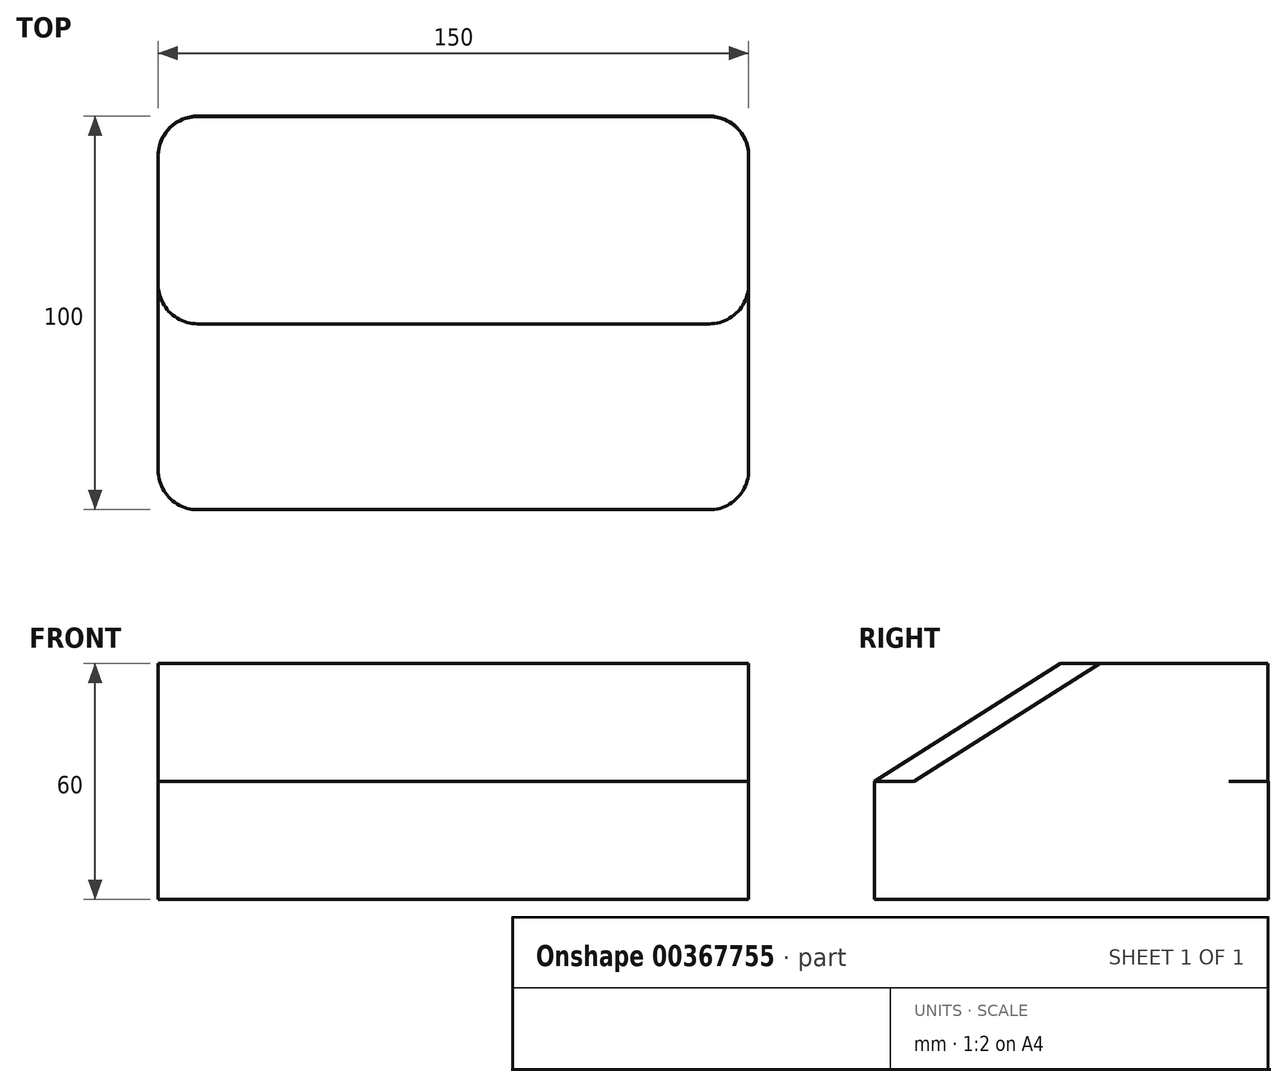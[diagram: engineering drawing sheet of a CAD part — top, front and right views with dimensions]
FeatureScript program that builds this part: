
annotation { "Feature Type Name" : "Feature", "Feature Type Description" : "" }
export const myFeature = defineFeature(function(context is Context, id is Id, definition is map)
    precondition{}
    {
        {
            var Q0;
            Q0=qCreatedBy(makeId("Top.planeOp"),FACE);
            var sketch = newSketch(context, id + "F0", { "sketchPlane" : qUnion([Q0])});
            skLineSegment(sketch, "E0.bottom", {"start": v(-67.57, 52.77) * mm, "end": v(62.43, 52.77) * mm});
            skLineSegment(sketch, "E0.top", {"start": v(-67.57, -47.23) * mm, "end": v(62.43, -47.23) * mm});
            skLineSegment(sketch, "E0.left", {"start": v(-77.57, 42.77) * mm, "end": v(-77.57, -37.23) * mm});
            skLineSegment(sketch, "E0.right", {"start": v(72.43, 42.77) * mm, "end": v(72.43, -37.23) * mm});
            skPoint(sketch, "E1.visualSharp", {"position": v(-77.57, 52.77) * mm});
            skArc(sketch, "E1.filletArc", {"start": v(-67.57, 52.77) * mm, "mid": v(-74.64, 49.85) * mm, "end": v(-77.57, 42.77) * mm});
            skPoint(sketch, "E2.visualSharp", {"position": v(72.43, 52.77) * mm});
            skArc(sketch, "E2.filletArc", {"start": v(72.43, 42.77) * mm, "mid": v(69.5, 49.85) * mm, "end": v(62.43, 52.77) * mm});
            skPoint(sketch, "E3.visualSharp", {"position": v(72.43, -47.23) * mm});
            skArc(sketch, "E3.filletArc", {"start": v(62.43, -47.23) * mm, "mid": v(69.5, -44.3) * mm, "end": v(72.43, -37.23) * mm});
            skPoint(sketch, "E4.visualSharp", {"position": v(-77.57, -47.23) * mm});
            skArc(sketch, "E4.filletArc", {"start": v(-77.57, -37.23) * mm, "mid": v(-74.64, -44.3) * mm, "end": v(-67.57, -47.23) * mm});
            skSolve(sketch);
        }
        {
            var Q0;
            Q0=makeQuery(id+"F0.imprint","IMPRINT",FACE,{"disambiguationData":[TD([[makeQuery(id+"F0.imprint","IMPRINT",EDGE,{"derivedFrom":sQuery(id+"F0.wireOp",EDGE,"E0.bottom")}),-1.0]])]});
            extrude(context, id + "F1", {"entities" : qUnion([Q0]), "depth" : 30 * mm});
        }
        {
            var Q0;
            Q0=makeQuery(id+"F1.opExtrude","CAP_FACE",FACE,{"disambiguationData":[OSD([sQuery(id+"F0.wireOp",EDGE,"E0.bottom"),sQuery(id+"F0.wireOp",EDGE,"E0.top"),sQuery(id+"F0.wireOp",EDGE,"E0.left"),sQuery(id+"F0.wireOp",EDGE,"E0.right"),sQuery(id+"F0.wireOp",EDGE,"E1.filletArc"),sQuery(id+"F0.wireOp",EDGE,"E2.filletArc"),sQuery(id+"F0.wireOp",EDGE,"E3.filletArc"),sQuery(id+"F0.wireOp",EDGE,"E4.filletArc")])],"isStart":false});
            var sketch = newSketch(context, id + "F2", { "sketchPlane" : qUnion([Q0])});
            skLineSegment(sketch, "E5.bottom", {"start": v(-67.57, 52.66) * mm, "end": v(62.43, 52.66) * mm});
            skLineSegment(sketch, "E5.top", {"start": v(-67.57, 0) * mm, "end": v(62.43, 0) * mm});
            skLineSegment(sketch, "E5.left", {"start": v(-77.57, 42.66) * mm, "end": v(-77.57, 10) * mm});
            skLineSegment(sketch, "E5.right", {"start": v(72.43, 42.66) * mm, "end": v(72.43, 10) * mm});
            skPoint(sketch, "E6.visualSharp", {"position": v(-77.57, 0) * mm});
            skArc(sketch, "E6.filletArc", {"start": v(-77.57, 10) * mm, "mid": v(-74.64, 2.93) * mm, "end": v(-67.57, 0) * mm});
            skPoint(sketch, "E7.visualSharp", {"position": v(72.43, 0) * mm});
            skArc(sketch, "E7.filletArc", {"start": v(62.43, 0) * mm, "mid": v(69.5, 2.93) * mm, "end": v(72.43, 10) * mm});
            skPoint(sketch, "E8.visualSharp", {"position": v(-77.57, 52.66) * mm});
            skArc(sketch, "E8.filletArc", {"start": v(-67.57, 52.66) * mm, "mid": v(-74.64, 49.73) * mm, "end": v(-77.57, 42.66) * mm});
            skPoint(sketch, "E9.visualSharp", {"position": v(72.43, 52.66) * mm});
            skArc(sketch, "E9.filletArc", {"start": v(72.43, 42.66) * mm, "mid": v(69.5, 49.73) * mm, "end": v(62.43, 52.66) * mm});
            skSolve(sketch);
        }
        {
            var Q0;
            {var subQ3=sQuery(id+"F2.wireOp",EDGE,"E5.top");Q0=makeQuery(id+"F2.imprint","IMPRINT",FACE,{"disambiguationData":[TD([[makeQuery(id+"F2.imprint","IMPRINT",EDGE,{"derivedFrom":subQ3}),1.0]])]});}
            extrude(context, id + "F3", {"entities" : qUnion([Q0]), "operationType" : NewBodyOperationType.ADD, "depth" : 30 * mm});
        }
        {
            var Q1;
            Q1=makeQuery(id+"F3.opExtrude","CAP_FACE",FACE,{"disambiguationData":[OSD([sQuery(id+"F2.wireOp",EDGE,"E5.bottom"),sQuery(id+"F2.wireOp",EDGE,"E5.top"),sQuery(id+"F2.wireOp",EDGE,"E5.left"),sQuery(id+"F2.wireOp",EDGE,"E5.right"),sQuery(id+"F2.wireOp",EDGE,"E6.filletArc"),sQuery(id+"F2.wireOp",EDGE,"E7.filletArc"),sQuery(id+"F2.wireOp",EDGE,"E8.filletArc"),sQuery(id+"F2.wireOp",EDGE,"E9.filletArc")])],"isStart":false});
            var Q2;
            {var subQ0=sQuery(id+"F0.wireOp",EDGE,"E0.right");var subQ1=sQuery(id+"F0.wireOp",EDGE,"E0.left");var subQ2=sQuery(id+"F0.wireOp",EDGE,"E3.filletArc");var subQ3=sQuery(id+"F0.wireOp",EDGE,"E0.top");var subQ4=sQuery(id+"F0.wireOp",EDGE,"E4.filletArc");Q2=makeQuery(id+"F3.boolean.opBoolean","SPLIT",FACE,{"disambiguationData":[TD([makeQuery(id+"F1.opExtrude","SWEPT_FACE",FACE,{"disambiguationData":[OSD([subQ3])]})])],"derivedFrom":makeQuery(id+"F1.opExtrude","CAP_FACE",FACE,{"disambiguationData":[OSD([sQuery(id+"F0.wireOp",EDGE,"E0.bottom"),subQ3,subQ1,subQ0,sQuery(id+"F0.wireOp",EDGE,"E1.filletArc"),sQuery(id+"F0.wireOp",EDGE,"E2.filletArc"),subQ2,subQ4])],"isStart":false})});}
            loft(context, id + "F4", {"operationType" : NewBodyOperationType.ADD, "sheetProfilesArray" : [{ "sheetProfileEntities" : qUnion([Q1]) }, { "sheetProfileEntities" : qUnion([Q2]) }]});
        }
        {
            var Q0;
            Q0=makeQuery(id+"F4.opLoft","SWEPT_FACE",FACE,{"disambiguationData":[OSD([sQuery(id+"F0.wireOp",EDGE,"E0.top"),sQuery(id+"F0.wireOp",EDGE,"E3.filletArc"),sQuery(id+"F0.wireOp",EDGE,"E4.filletArc"),sQuery(id+"F2.wireOp",EDGE,"E5.top"),sQuery(id+"F2.wireOp",EDGE,"E6.filletArc"),sQuery(id+"F2.wireOp",EDGE,"E7.filletArc")])]});
            var sketch = newSketch(context, id + "F5", { "sketchPlane" : qUnion([Q0])});
            skLineSegment(sketch, "E10.bottom", {"start": v(-57.57, 22.17) * mm, "end": v(52.43, 22.17) * mm, "construction": true});
            skLineSegment(sketch, "E10.top", {"start": v(-57.57, -13.78) * mm, "end": v(52.43, -13.78) * mm, "construction": true});
            skLineSegment(sketch, "E10.left", {"start": v(-57.57, 22.17) * mm, "end": v(-57.57, -13.78) * mm, "construction": true});
            skLineSegment(sketch, "E10.right", {"start": v(52.43, 22.17) * mm, "end": v(52.43, -13.78) * mm, "construction": true});
            skLineSegment(sketch, "E11", {"start": v(-57.57, 4.2) * mm, "end": v(52.43, 4.2) * mm, "construction": true});
            skCircle(sketch, "E12", {"center": v(-27.57, -13.78) * mm, "radius": 1.5 * mm});
            skCircle(sketch, "E13", {"center": v(-2.57, -13.78) * mm, "radius": 1.5 * mm});
            skCircle(sketch, "E14", {"center": v(22.43, -13.78) * mm, "radius": 1.5 * mm});
            skCircle(sketch, "E15", {"center": v(47.43, -13.78) * mm, "radius": 1.5 * mm});
            skCircle(sketch, "E16", {"center": v(-52.57, -13.78) * mm, "radius": 1.5 * mm});
            skSolve(sketch);
        }
        {
            var Q0;
            Q0=sQuery(id+"F5.wireOp",EDGE,"E15");
            var Q1;
            Q1=sQuery(id+"F5.wireOp",EDGE,"E14");
            var Q2;
            Q2=sQuery(id+"F5.wireOp",EDGE,"E13");
            var Q3;
            Q3=sQuery(id+"F5.wireOp",EDGE,"E12");
            var Q4;
            Q4=sQuery(id+"F5.wireOp",EDGE,"E16");
            extrude(context, id + "F6", {"bodyType" : ToolBodyType.SURFACE, "operationType" : NewBodyOperationType.REMOVE, "surfaceEntities" : qUnion([Q0, Q1, Q2, Q3, Q4]), "oppositeDirection" : true, "depth" : 25 * mm});
        }
        {
            var Q0;
            Q0=makeQuery(id+"F6.opExtrude","SWEPT_BODY",BODY,{"disambiguationData":[OSD([sQuery(id+"F5.wireOp",EDGE,"E16")])]});
            deleteBodies(context, id + "F7", {"entities" : qUnion([Q0])});
        }
        {
            var Q0;
            Q0=makeQuery(id+"F6.opExtrude","SWEPT_BODY",BODY,{"disambiguationData":[OSD([sQuery(id+"F5.wireOp",EDGE,"E15")])]});
            deleteBodies(context, id + "F8", {"entities" : qUnion([Q0])});
        }
        {
            var Q0;
            Q0=makeQuery(id+"F6.opExtrude","SWEPT_BODY",BODY,{"disambiguationData":[OSD([sQuery(id+"F5.wireOp",EDGE,"E14")])]});
            deleteBodies(context, id + "F9", {"entities" : qUnion([Q0])});
        }
        {
            var Q0;
            Q0=makeQuery(id+"F6.opExtrude","SWEPT_BODY",BODY,{"disambiguationData":[OSD([sQuery(id+"F5.wireOp",EDGE,"E13")])]});
            deleteBodies(context, id + "F10", {"entities" : qUnion([Q0])});
        }
        {
            var Q0;
            Q0=makeQuery(id+"F6.opExtrude","SWEPT_BODY",BODY,{"disambiguationData":[OSD([sQuery(id+"F5.wireOp",EDGE,"E12")])]});
            deleteBodies(context, id + "F11", {"entities" : qUnion([Q0])});
        }
    });
